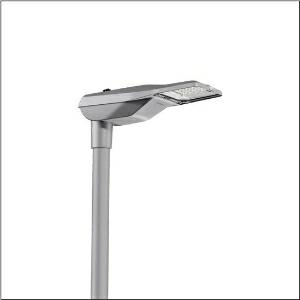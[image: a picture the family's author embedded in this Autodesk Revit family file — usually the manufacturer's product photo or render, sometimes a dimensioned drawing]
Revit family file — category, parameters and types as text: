
# Revit family: streetlight_sl_21_iq_micro___p0_8a_5xe1u31v08cb_453e
name_source: partatom
category: Lighting Fixtures
units: mm (PartAtom-declared; Revit-internal decimal feet)

## family parameters
Cut with Voids When Loaded = No
Host = Face
Light Source = No
Part Type = Normal
Room Calculation Point = No
Round Connector Dimension = Use Diameter
Shared = No

## types (1)
- --- (1 x LED, 2890 lm, 19.1 W, 3000K)
    Apparent Load = 19 VA
    CIE Flux Codes = 33 69 96 100 100
    Color Rendering = 70
    Color Temperature = 3000K
    Default Elevation = 1800 mm
    Description = Streetlight SL 21 iQ micro, mast luminaire, primary light control with lens, of PMMA, primary optical cover: cover, of toughened safety glass, transparent, light distribution: P0.8a, light emission: direct distribution, primary light characteristic: asymmetric, installation type: post-top, side-entry, LED, High Power LED, rated luminous flux: 2.890lm, luminous efficacy: 151lm/W, light colour: 730, colour temperature: 3000K, control gear: iQ-Street Remote, D4i with power reduction, control: pre-setting: logarithmic dimming characteristic, Street-Remote, Auto-Match, Temp-Guard, Lumen-Switch, Night-Set, Smart-Wire, Light-Fading, Desk-Remote (wireless, voltage-free reading and setting of iQ features in the workshop via application-optimized NFC function/RFID function), optimised constant luminous flux control (CLO 2.0), mains connection: 220..240V, AC, 50/60Hz, start of lifetime: 19W, end of service life: 20W, reduction: 9W, luminaire housing, of diecast aluminium, powder-coated, Siteco® metallic grey (DB 702S), corrosivity category C5 mid according to DIN EN ISO 12944, please order mast flange separately, inclination adjustable: 0°, 5°, 10°, 15°, sealing non-destructively replaceable, multi-level sealing system, length: 528mm, width: 235mm, height: 110mm, mast flange for spigot size: 42mm (side-entry): 5XC10008XM4, 60/48mm (side-entry/post-top): 5XC10108XM2, 76/60mm (side-entry/post-top): 5XC10108XM1, mounting height: 4..8m, Smart Interface above, protection rating (complete): IP66, insulation class (complete): insulation class II (safety insulation), certification: CE, ENEC, ENEC+, VDE, impact resistance: IK10, permissible operating ambient temperature for outdoor applications: -40..+50°C, standard-compliant lighting for roads and squares, packaging unit: 1 piece

Light Distribution: P0.8a
    Height = 110 mm
    Lamp = 1 x LED
    Lamp Light Flux = 2890 lm
    Lamp Power = 19.1 W
    Lamp count = 1
    Length = 528 mm
    Luminous efficacy = 151 lm/W
    Manufacturer = Siteco
    ModVariant = No
    Model = 5XE1U31V08CB
    Number of Poles = 1
    OnlyDefault = Yes
    Power Factor = 1
    Product Name = Streetlight SL 21 iQ micro | P0.8a
    Product group = mast luminaire | pylon top
    ProductGroupID = 6100
    Protection Class = Protection class II
    Protection Degree = IP 66
    RLX_Detail_Level = 1
    RLX_Emergency_Light_Flux = 0 lm
    RLX_Emergency_Type = 0
    RLX_Emergency_Type_DB = No
    RlxData = <blob elided: 98185 chars, md5=fa59d692>
    Socket = socket
    Standby Power = 0 W
    System Light Flux = 2890 lm
    System Power = 19 W
    Type Comments = factory setting: luminous flux: 100 % | dim-lin: 254 | 387 mA
    Type Image = l_1277292.jpg
    URL = http://relux.com
    VarID = @adj_072928
    Voltage = 0 V
    Weight = 0.00 kg
    Width = 235 mm

## geometry (parser evidence)
native form markers: Blend x4, Sweep x10
no freeform markers — native parametric forms only
